# Revit family: Detail-Bolt Assembly-ISO Metric-Hexagon-Top_Temp_c04fe1ba-34a2-4746-b298-63dc00aedf6d
name_source: partatom
category: Detail Items
revit_build: Autodesk Revit 2016 (Build: 20160314_0715(x64)
units: mm (PartAtom-declared; Revit-internal decimal feet)

## family parameters
OmniClass Number = 23.20.40.11.14.27
OmniClass Title = Bolts and Nuts
Rotate with component = No
Shared = No

## types (1)
- M16
    Bolt Diameter = 16 mm  [stored 0.0524934 ft]
    CBICode = 3411
    CBIDescription = Structural steelwork
    Centreline Size = 48 mm  [stored 0.15748 ft]
    Description = ISO Metric Precision Hexagon Bolt in accordance with BS 3692:2001
    Manufacturer = Steel & Tube
    ManufacturerName = Steel & Tube
    ManufacturerURL = http://www.steelandtube.co.nz
    Model = M16
    ModifiedIssue_ANZRS = 20160520 $
    Nut Size = 24 mm  [stored 0.0787402 ft]
    SpecificationDescription = Steel & Tube Purlins & Girts
    SpecificationReference = 3411ST
    Type Comments = Top View
    URL = http://www.steelandtube.co.nz
    Uniclass2015Code = Pr_20_76_51_21
    Uniclass2015Title = Cold-formed galvanized steel sections
    Uniclass2015Version = 2015

note: [stored X ft] marks values corroborated as IEEE doubles in the binary element streams (Revit-internal decimal feet)

## geometry (parser evidence)
native form markers: Sweep x1
no freeform markers — native parametric forms only
